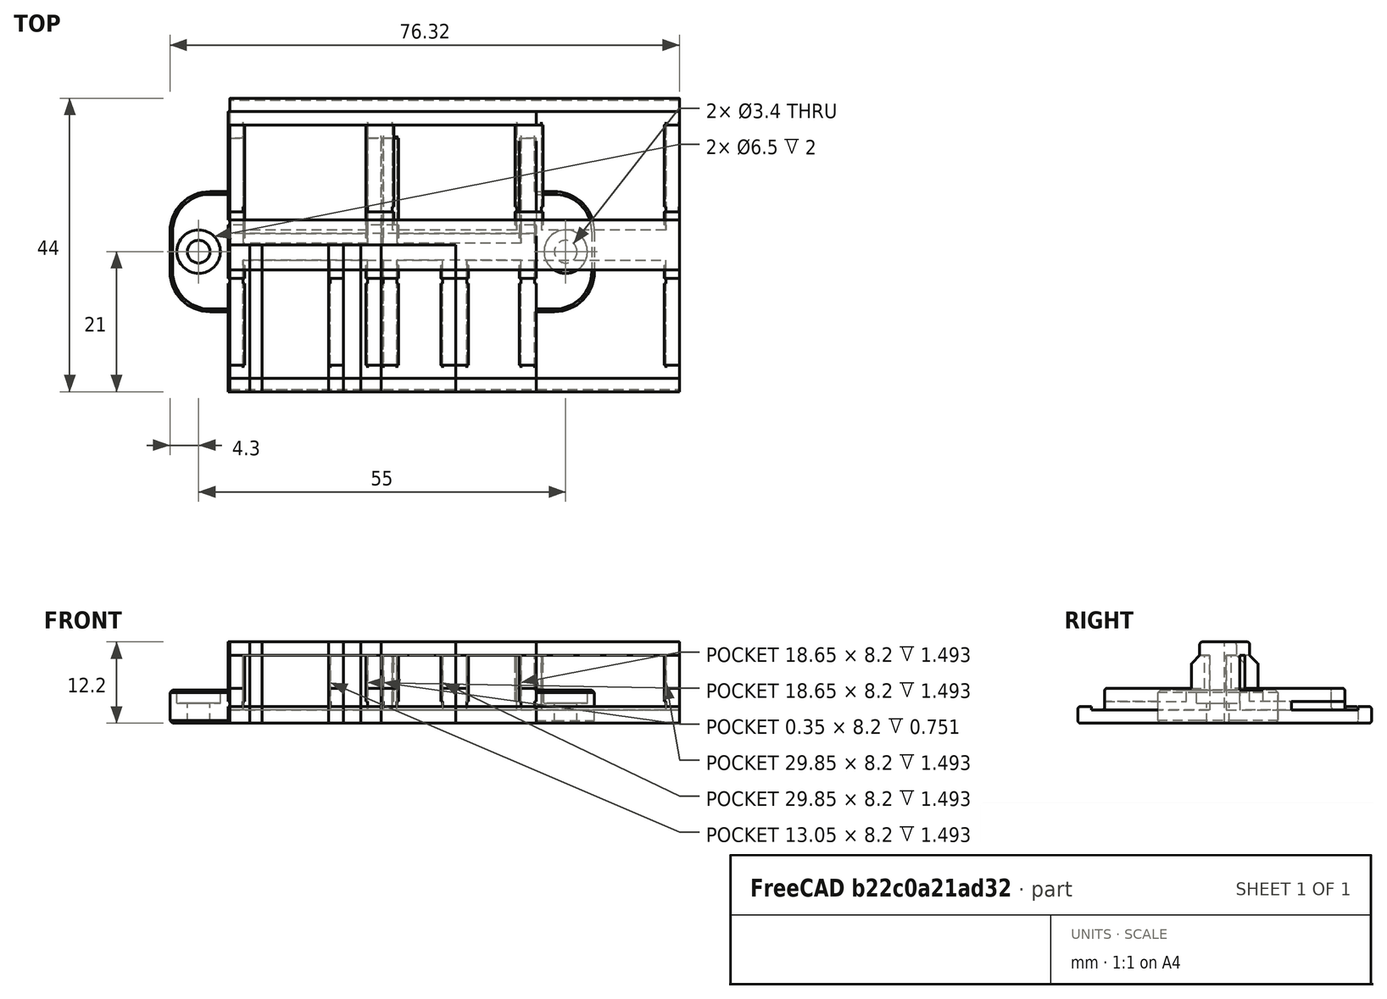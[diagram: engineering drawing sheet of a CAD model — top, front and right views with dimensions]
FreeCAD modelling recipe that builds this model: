
FCSTD DOCUMENT  (FreeCAD 0.19R24291 (Git))
Label: wago-mount
License: Other
LicenseURL: GPL3
objects: Part::Feature×20, Part::MultiFuse×4, Part::Box×3, Part::MultiCommon×3, Part::Extrusion×3, Spreadsheet::Sheet×1
note: 33 computed .brp shape members not serialized (recipe doc carries the construction recipe); baked Part::Feature solids carry a one-line shape summary decoded from their .brp

FEATURE [Part::Feature] Cut009001  label="wago-mount"
  Placement = pos=(19,21,1.9e-14) rot=(0,0,1;4.71239rad)
  shape: bbox 63.6 x 41.99 x 12.2 mm, 224 faces (baked)
FEATURE [Part::Box] Box  label="Cube"
  AttacherType = Attacher::AttachEngine3D
  Height = 15
  Length = 3
  Placement = pos=(-4.83,0,0) rot=(0,0,1;0rad)
  Width = 22
FEATURE [Part::Box] Box001  label="Cube001"
  AttacherType = Attacher::AttachEngine3D
  Height = 15
  Length = 3
  Placement = pos=(14.82,0,0) rot=(0,0,1;0rad)
  Width = 22
FEATURE [Part::Box] Box002  label="Cube002"
  AttacherType = Attacher::AttachEngine3D
  Height = 15
  Length = 10
  Width = 22
FEATURE [Part::Feature] Cut009002  label="wago-mount001"
  Placement = pos=(19,21,1.9e-14) rot=(0,0,-1;1.5708rad)
  shape: bbox 63.6 x 41.99 x 12.2 mm, 224 faces (baked)
FEATURE [Part::Feature] Cut009003  label="wago-mount002"
  Placement = pos=(19,21,1.9e-14) rot=(0,0,-1;1.5708rad)
  shape: bbox 63.6 x 41.99 x 12.2 mm, 224 faces (baked)
FEATURE [Part::Feature] Cut009004  label="wago-mount003"
  Placement = pos=(19,21,1.9e-14) rot=(0,0,-1;1.5708rad)
  shape: bbox 63.6 x 41.99 x 12.2 mm, 224 faces (baked)
FEATURE [Part::MultiCommon] Common  label="left"
  Shapes = -> [Cut009002,Box]
FEATURE [Part::MultiCommon] Common001  label="right"
  Shapes = -> [Cut009003,Box001]
FEATURE [Part::MultiCommon] Common002  label="mid"
  Shapes = -> [Cut009004,Box002]
FEATURE [Part::Feature] Common002_cs  label="mid-profile"
  shape: bbox 5e-07 x 22 x 12.2 mm, 0 faces, 0 solids (baked)
FEATURE [Part::Feature] Common003  label="left001"
  shape: bbox 3 x 22 x 12.2 mm, 39 faces (baked)
FEATURE [Part::Feature] Common001001  label="right001"
  shape: bbox 3 x 22 x 12.2 mm, 29 faces (baked)
FEATURE [Part::Feature] Common002_cs001  label="mid-profile001"
  shape: bbox 5e-07 x 22 x 12.2 mm, 0 faces, 0 solids (baked)
FEATURE [Spreadsheet::Sheet] Spreadsheet
  cells = A1=spacing; B1=5.6
FEATURE [Part::Feature] Common002_cs002  label="mid-profile002"
  shape: bbox 5e-07 x 22 x 12.2 mm, 0 faces, 0 solids (baked)
FEATURE [Part::Feature] Common002_cs003  label="mid-profile003"
  shape: bbox 5e-07 x 22 x 12.2 mm, 0 faces, 0 solids (baked)
FEATURE [Part::Extrusion] Extrude  label="mid-3"
  Base = -> Common002_cs001
  Dir = (1,0,0)
  DirMode = 2
  FaceMakerClass = Part::FaceMakerBullseye
  LengthFwd = 18.65
  LengthRev = 0
  Placement = pos=(-7.58,0,0) rot=(0,0,1;0rad)
  Solid = true
  Symmetric = false
FEATURE [Part::Extrusion] Extrude001  label="mid-2"
  Base = -> Common002_cs002
  Dir = (1,0,0)
  DirMode = 2
  FaceMakerClass = Part::FaceMakerBullseye
  LengthFwd = 13.05
  LengthRev = 0
  Placement = pos=(-7.58,0,0) rot=(0,0,1;0rad)
  Solid = true
  Symmetric = false
FEATURE [Part::Extrusion] Extrude002  label="mid-5"
  Base = -> Common002_cs003
  Dir = (1,0,0)
  DirMode = 2
  FaceMakerClass = Part::FaceMakerBullseye
  LengthFwd = 29.85
  LengthRev = 0
  Placement = pos=(-7.58,0,0) rot=(0,0,1;0rad)
  Solid = true
  Symmetric = false
FEATURE [Part::MultiFuse] Fusion  label="slot-3-template"
  Refine = true
  Shapes = -> [Extrude,Common001001,Common003]
FEATURE [Part::Feature] Common001002  label="right002"
  Placement = pos=(-5.6,0,0) rot=(0,0,1;0rad)
  shape: bbox 3 x 22 x 12.2 mm, 29 faces (baked)
FEATURE [Part::Feature] Common001003  label="left002"
  shape: bbox 3 x 22 x 12.2 mm, 39 faces (baked)
FEATURE [Part::MultiFuse] Fusion001  label="slot-2-template"
  Refine = true
  Shapes = -> [Extrude001,Common001003,Common001002]
FEATURE [Part::Feature] Common001004  label="right003"
  Placement = pos=(11.2,0,0) rot=(0,0,1;0rad)
  shape: bbox 3 x 22 x 12.2 mm, 29 faces (baked)
FEATURE [Part::Feature] Common001005  label="left003"
  shape: bbox 3 x 22 x 12.2 mm, 39 faces (baked)
FEATURE [Part::MultiFuse] Fusion002  label="slot-5-template"
  Refine = true
  Shapes = -> [Extrude002,Common001004,Common001005]
FEATURE [Part::Feature] Fusion002001  label="slot-5-template001"
  shape: bbox 33.85 x 22 x 12.2 mm, 53 faces (baked)
FEATURE [Part::Feature] Fusion002002  label="slot-3-template001"
  Placement = pos=(13,44,0) rot=(0,0,-1;3.14159rad)
  shape: bbox 22.65 x 22 x 12.2 mm, 53 faces (baked)
FEATURE [Part::Feature] Fusion002003  label="slot-5-template002"
  Placement = pos=(33.5,0,0) rot=(0,0,1;0rad)
  shape: bbox 33.85 x 22 x 12.2 mm, 53 faces (baked)
FEATURE [Part::Feature] Fusion002004  label="slot-3-template002"
  Placement = pos=(57.69,44,0) rot=(0,0,1;3.14159rad)
  shape: bbox 22.65 x 22 x 12.2 mm, 53 faces (baked)
FEATURE [Part::Feature] Fusion002005  label="slot-3-template003"
  Placement = pos=(35.345,44,0) rot=(0,0,1;3.14159rad)
  shape: bbox 22.65 x 22 x 12.2 mm, 53 faces (baked)
FEATURE [Part::MultiFuse] Fusion002006  label="33355-mount"
  Refine = true
  Shapes = -> [Fusion002001,Fusion002002,Fusion002003,Fusion002004,Fusion002005]
FEATURE [Part::Feature] Fusion002006001  label="33355-mount001"
  shape: bbox 67.35 x 43.99 x 12.2 mm, 171 faces (baked)
